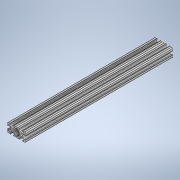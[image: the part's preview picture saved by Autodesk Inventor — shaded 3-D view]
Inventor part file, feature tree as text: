
AUTODESK INVENTOR PART (.ipt)
format: ipt  version: 2020 (Build 240168000, 168)  size: 333,824 bytes
history: native  units: in
note: dims shown in document units (in); Inventor stores cm internally (conversion verified against a paired STEP export)
features: sketch x2, extrude x1
ambient origin geometry x8: Origin, YZ Plane, XZ Plane, XY Plane, X Axis, Y Axis, Z Axis, Center Point
bodies: Solid1 (feature_tree)
feature tree (3):
  extrude  "Extrusion1"  [1 undecoded]
  sketch  "Sketch2"
  sketch  "Sketch1"  dims[d0=16.0in d1=0.0in]
note: 1 required parameter value undecoded (feature->parameter linkage not recoverable at this tier; creation-order binding heuristic only, values carry confidence <= 0.55)
